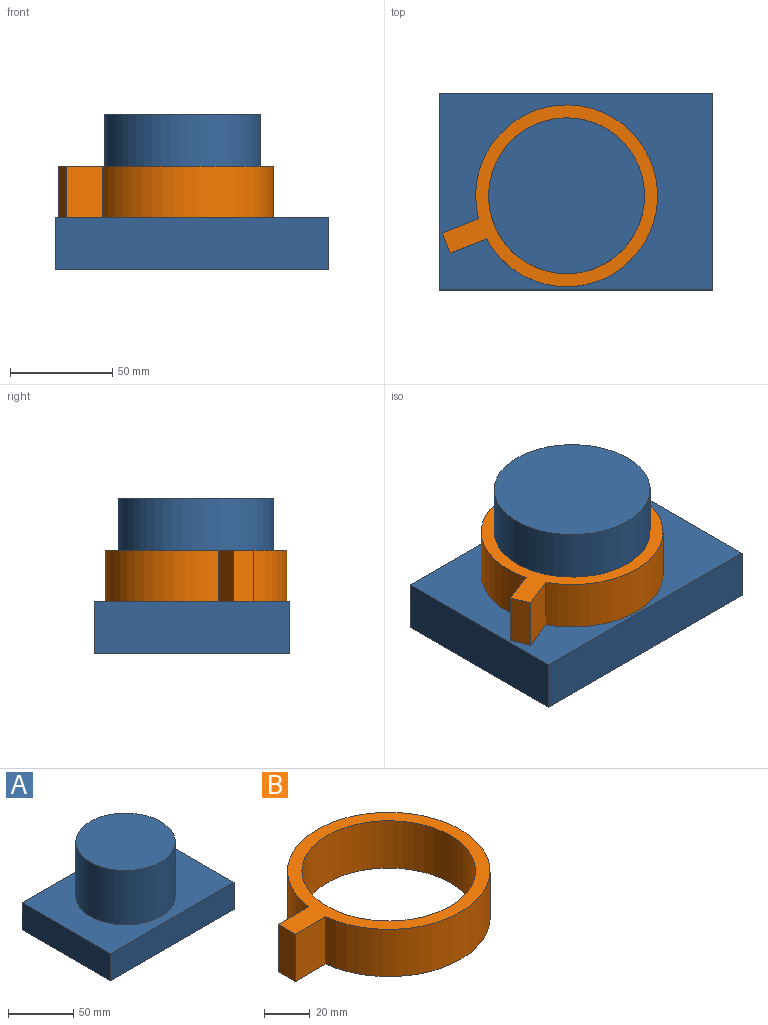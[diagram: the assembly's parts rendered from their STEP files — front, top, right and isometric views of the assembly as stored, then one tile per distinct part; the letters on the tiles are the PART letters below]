
ASSEMBLY  parts=2 mates=1
PART A: 8 faces, bbox 133.7x95.8x76.2 mm
  f0: cylinder r=38.1mm len=76.2mm, axis (0,0,-1), area 12161mm2, adj f1,f7
  f1: plane 76.2x76.2mm, normal (0,0,1), area 4560.4mm2, adj f0
  f2: plane 133.72x25.4mm, normal (0,-1,0), area 3396.5mm2, adj f3,f5,f6,f7
  f3: plane 95.77x25.4mm, normal (-1,0,0), area 2432.4mm2, adj f2,f4,f6,f7
  f4: plane 133.72x25.4mm, normal (0,1,0), area 3396.5mm2, adj f3,f5,f6,f7
  f5: plane 95.77x25.4mm, normal (1,0,0), area 2432.4mm2, adj f2,f4,f6,f7
  f6: plane 133.72x95.77mm, normal (0,0,-1), area 12805.8mm2, adj f2,f3,f4,f5
  f7: plane 133.72x95.77mm, normal (0,0,1), area 8245.4mm2, adj f0,f2,f3,f4,f5
PART B: 7 faces, bbox 107.6x88.9x25.4 mm
  f0: plane 25.4x18.98mm, normal (0,-1,0), area 482.1mm2, adj f1,f3,f5,f6
  f1: cylinder r=44.45mm len=88.9mm, axis (0,0,-1), area 6824.1mm2, adj f0,f2,f5,f6
  f2: plane 25.4x19.04mm, normal (0,1,0), area 483.7mm2, adj f1,f3,f5,f6
  f3: plane 25.4x10.6mm, normal (-1,0,0), area 269.1mm2, adj f0,f2,f5,f6
  f4: cylinder r=38.1mm len=76.2mm, axis (0,0,-1), area 6080.5mm2, adj f5,f6
  f5: plane 107.6x88.9mm, normal (0,0,1), area 1846mm2, adj f0,f1,f2,f3,f4
  f6: plane 107.6x88.9mm, normal (0,0,-1), area 1846mm2, adj f0,f1,f2,f3,f4
PLACE A t=(64.75,-37.02,-11.06)mm fixed
PLACE B rot(axis=(0,0,1),21.7deg) t=(64.75,-37.02,-11.06)mm
MATE cylindrical B.f4 <-> A.f0  axis (0,0,-1) through (64.75,-37.02,14.34)mm
